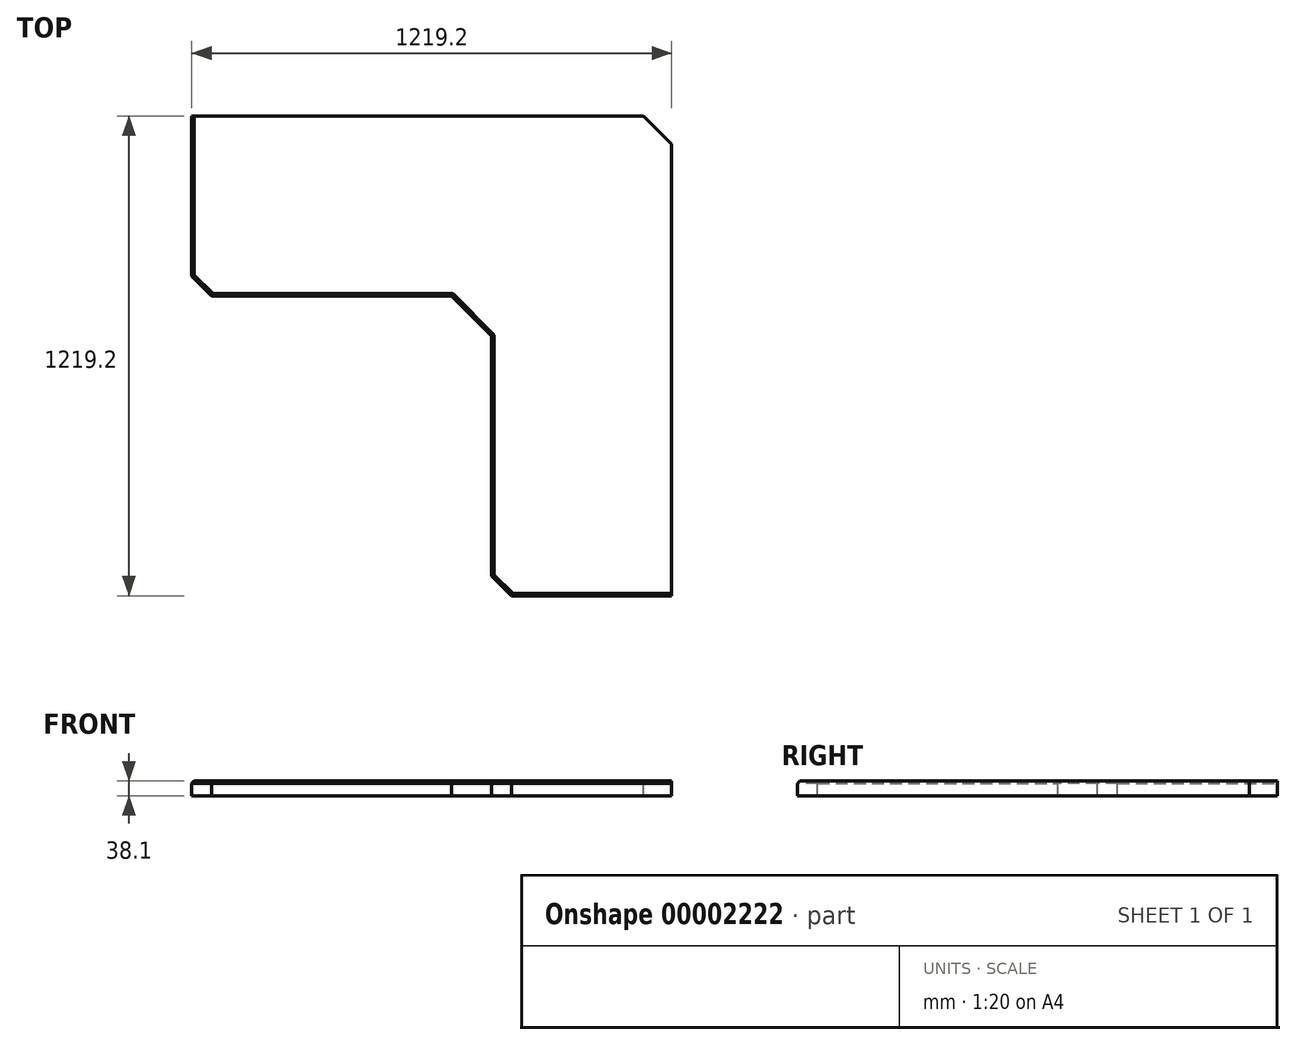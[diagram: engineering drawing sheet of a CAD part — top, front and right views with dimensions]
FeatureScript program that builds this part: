
annotation { "Feature Type Name" : "Feature", "Feature Type Description" : "" }
export const myFeature = defineFeature(function(context is Context, id is Id, definition is map)
    precondition{}
    {
        {
            var Q0;
            Q0=qCreatedBy(makeId("Top.planeOp"),FACE);
            var sketch = newSketch(context, id + "F0", { "sketchPlane" : qUnion([Q0])});
            skLineSegment(sketch, "E0", {"start": v(0, 0) * mm, "end": v(-1219.2, 0) * mm});
            skLineSegment(sketch, "E1", {"start": v(-1219.2, 0) * mm, "end": v(-1219.2, -457.2) * mm});
            skLineSegment(sketch, "E2", {"start": v(-1219.2, -457.2) * mm, "end": v(-457.2, -457.2) * mm});
            skLineSegment(sketch, "E3", {"start": v(-457.2, -457.2) * mm, "end": v(-457.2, -1219.2) * mm});
            skLineSegment(sketch, "E4", {"start": v(-457.2, -1219.2) * mm, "end": v(0, -1219.2) * mm});
            skLineSegment(sketch, "E5", {"start": v(0, -1219.2) * mm, "end": v(0, 0) * mm});
            skSolve(sketch);
        }
        {
            var Q0;
            Q0=makeQuery(id+"F0.imprint","IMPRINT",FACE,{"disambiguationData":[TD([[makeQuery(id+"F0.imprint","IMPRINT",EDGE,{"derivedFrom":sQuery(id+"F0.wireOp",EDGE,"E0")}),1.0]])]});
            extrude(context, id + "F1", {"entities" : qUnion([Q0]), "depth" : 38.1 * mm});
        }
        {
            var Q0;
            Q0=makeQuery(id+"F1.opExtrude","CAP_FACE",FACE,{"disambiguationData":[OSD([sQuery(id+"F0.wireOp",EDGE,"E0"),sQuery(id+"F0.wireOp",EDGE,"E1"),sQuery(id+"F0.wireOp",EDGE,"E2"),sQuery(id+"F0.wireOp",EDGE,"E3"),sQuery(id+"F0.wireOp",EDGE,"E4"),sQuery(id+"F0.wireOp",EDGE,"E5")])],"isStart":false});
            var sketch = newSketch(context, id + "F2", { "sketchPlane" : qUnion([Q0])});
            skLineSegment(sketch, "E6", {"start": v(-71.84, 0) * mm, "end": v(0, -71.84) * mm});
            skSolve(sketch);
        }
        {
            var Q0;
            {var subQ1=sQuery(id+"F2.wireOp",EDGE,"E6");Q0=makeQuery(id+"F2.imprint","IMPRINT",FACE,{"disambiguationData":[TD([[makeQuery(id+"F2.imprint","IMPRINT",EDGE,{"derivedFrom":subQ1}),1.0]])]});}
            extrude(context, id + "F3", {"entities" : qUnion([Q0]), "operationType" : NewBodyOperationType.REMOVE, "endBound" : BoundingType.THROUGH_ALL, "oppositeDirection" : true, "depth" : 25.4 * mm});
        }
        {
            var Q0;
            Q0=makeQuery(id+"F1.opExtrude","SWEPT_EDGE",EDGE,{"disambiguationData":[OSD([sQuery(id+"F0.wireOp",EDGE,"E1"),sQuery(id+"F0.wireOp",EDGE,"E2")])]});
            var Q1;
            Q1=makeQuery(id+"F1.opExtrude","SWEPT_EDGE",EDGE,{"disambiguationData":[OSD([sQuery(id+"F0.wireOp",EDGE,"E3"),sQuery(id+"F0.wireOp",EDGE,"E4")])]});
            chamfer(context, id + "F4", {"entities" : qUnion([Q0, Q1]), "width" : 50.8 * mm, "tangentPropagation" : true});
        }
        {
            var Q0;
            Q0=makeQuery(id+"F1.opExtrude","SWEPT_EDGE",EDGE,{"disambiguationData":[OSD([sQuery(id+"F0.wireOp",EDGE,"E2"),sQuery(id+"F0.wireOp",EDGE,"E3")])]});
            chamfer(context, id + "F5", {"entities" : qUnion([Q0]), "width" : 101.6 * mm, "tangentPropagation" : true});
        }
        {
            var Q0;
            Q0=makeQuery(id+"F1.opExtrude","CAP_FACE",FACE,{"disambiguationData":[OSD([sQuery(id+"F0.wireOp",EDGE,"E0"),sQuery(id+"F0.wireOp",EDGE,"E1"),sQuery(id+"F0.wireOp",EDGE,"E2"),sQuery(id+"F0.wireOp",EDGE,"E3"),sQuery(id+"F0.wireOp",EDGE,"E4"),sQuery(id+"F0.wireOp",EDGE,"E5")])],"isStart":false});
            var sketch = newSketch(context, id + "F6", { "sketchPlane" : qUnion([Q0])});
            skLineSegment(sketch, "E7", {"start": v(-207.78, 0) * mm, "end": v(0, -207.78) * mm});
            skLineSegment(sketch, "E8", {"start": v(-369.42, 0) * mm, "end": v(0, -369.42) * mm});
            skLineSegment(sketch, "E9", {"start": v(-531.07, 0) * mm, "end": v(0, -531.07) * mm});
            skLineSegment(sketch, "E10", {"start": v(-692.71, 0) * mm, "end": v(0, -692.71) * mm});
            skLineSegment(sketch, "E11", {"start": v(-854.36, 0) * mm, "end": v(0, -854.36) * mm});
            skLineSegment(sketch, "E12", {"start": v(-1016, 0) * mm, "end": v(0, -1016) * mm});
            skSolve(sketch);
        }
        {
            var Q0;
            Q0=makeQuery(id+"F1.opExtrude","CAP_EDGE",EDGE,{"disambiguationData":[OSD([sQuery(id+"F0.wireOp",EDGE,"E1")])],"isStart":false});
            var Q1;
            {var subQ0=sQuery(id+"F0.wireOp",EDGE,"E1");var subQ1=sQuery(id+"F0.wireOp",EDGE,"E2");Q1=makeQuery(id+"F4.opChamfer","BLEND_EDGE",EDGE,{"blendedFrom":[makeQuery(id+"F1.opExtrude","SWEPT_EDGE",EDGE,{"disambiguationData":[OSD([subQ0,subQ1])]}),makeQuery(id+"F1.opExtrude","CAP_FACE",FACE,{"disambiguationData":[OSD([sQuery(id+"F0.wireOp",EDGE,"E0"),subQ0,subQ1,sQuery(id+"F0.wireOp",EDGE,"E3"),sQuery(id+"F0.wireOp",EDGE,"E4"),sQuery(id+"F0.wireOp",EDGE,"E5")])],"isStart":false})],"blendedInto":[makeQuery(id+"F1.opExtrude","CAP_FACE",FACE,{"disambiguationData":[OSD([sQuery(id+"F0.wireOp",EDGE,"E0"),subQ0,subQ1,sQuery(id+"F0.wireOp",EDGE,"E3"),sQuery(id+"F0.wireOp",EDGE,"E4"),sQuery(id+"F0.wireOp",EDGE,"E5")])],"isStart":false})]});}
            var Q2;
            Q2=makeQuery(id+"F1.opExtrude","CAP_EDGE",EDGE,{"disambiguationData":[OSD([sQuery(id+"F0.wireOp",EDGE,"E2")])],"isStart":false});
            var Q3;
            Q3=makeQuery(id+"F1.opExtrude","CAP_EDGE",EDGE,{"disambiguationData":[OSD([sQuery(id+"F0.wireOp",EDGE,"E3")])],"isStart":false});
            var Q4;
            {var subQ0=sQuery(id+"F0.wireOp",EDGE,"E3");var subQ1=sQuery(id+"F0.wireOp",EDGE,"E4");Q4=makeQuery(id+"F4.opChamfer","BLEND_EDGE",EDGE,{"blendedFrom":[makeQuery(id+"F1.opExtrude","SWEPT_EDGE",EDGE,{"disambiguationData":[OSD([subQ0,subQ1])]}),makeQuery(id+"F1.opExtrude","CAP_FACE",FACE,{"disambiguationData":[OSD([sQuery(id+"F0.wireOp",EDGE,"E0"),sQuery(id+"F0.wireOp",EDGE,"E1"),sQuery(id+"F0.wireOp",EDGE,"E2"),subQ0,subQ1,sQuery(id+"F0.wireOp",EDGE,"E5")])],"isStart":false})],"blendedInto":[makeQuery(id+"F1.opExtrude","CAP_FACE",FACE,{"disambiguationData":[OSD([sQuery(id+"F0.wireOp",EDGE,"E0"),sQuery(id+"F0.wireOp",EDGE,"E1"),sQuery(id+"F0.wireOp",EDGE,"E2"),subQ0,subQ1,sQuery(id+"F0.wireOp",EDGE,"E5")])],"isStart":false})]});}
            var Q5;
            Q5=makeQuery(id+"F1.opExtrude","CAP_EDGE",EDGE,{"disambiguationData":[OSD([sQuery(id+"F0.wireOp",EDGE,"E4")])],"isStart":false});
            var Q6;
            {var subQ0=sQuery(id+"F0.wireOp",EDGE,"E2");var subQ1=sQuery(id+"F0.wireOp",EDGE,"E3");Q6=makeQuery(id+"F5.opChamfer","BLEND_EDGE",EDGE,{"blendedFrom":[makeQuery(id+"F1.opExtrude","SWEPT_EDGE",EDGE,{"disambiguationData":[OSD([subQ0,subQ1])]}),makeQuery(id+"F1.opExtrude","CAP_FACE",FACE,{"disambiguationData":[OSD([sQuery(id+"F0.wireOp",EDGE,"E0"),sQuery(id+"F0.wireOp",EDGE,"E1"),subQ0,subQ1,sQuery(id+"F0.wireOp",EDGE,"E4"),sQuery(id+"F0.wireOp",EDGE,"E5")])],"isStart":false})],"blendedInto":[makeQuery(id+"F1.opExtrude","CAP_FACE",FACE,{"disambiguationData":[OSD([sQuery(id+"F0.wireOp",EDGE,"E0"),sQuery(id+"F0.wireOp",EDGE,"E1"),subQ0,subQ1,sQuery(id+"F0.wireOp",EDGE,"E4"),sQuery(id+"F0.wireOp",EDGE,"E5")])],"isStart":false})]});}
            chamfer(context, id + "F7", {"entities" : qUnion([Q0, Q1, Q2, Q3, Q4, Q5, Q6]), "width" : 6.35 * mm, "tangentPropagation" : true});
        }
    });
